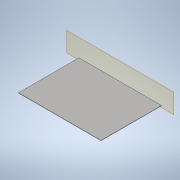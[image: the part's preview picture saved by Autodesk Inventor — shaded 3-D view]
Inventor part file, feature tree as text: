
AUTODESK INVENTOR PART (.ipt)
format: ipt  version: 2022.2 (Build 262287010, 287A)  size: 117,248 bytes
history: native  units: mm
features: reference x7, other x4, plane x2, sketch x1, extrude x1
ambient origin geometry x8: Origin, YZ Plane, XZ Plane, XY Plane, X Axis, Y Axis, Z Axis, Center Point
bodies: Volumenkörper1 (feature_tree)
feature tree (15):
  plane  "Arbeitsebene1"
  sketch  "Skizze1"  dims[d0=0.5mm d1=0.5mm d2=1.25mm d3=0.5mm d4=10.0mm d5=0.0mm]
  plane  "Arbeitsebene2"
  extrude  "Extrusion1"  Depth=1.25mm
  reference  "Referenz1"
  reference  "Referenz2"
  reference  "Referenz3"
  reference  "Referenz4"
  reference  "Referenz5"
  reference  "Referenz6"
  reference  "Referenz7"
  other  "Case_Assembly.iam"
  other  "Case_Side:2"
  other  "Case_Front:1"
  other  "Case_Side:1"
